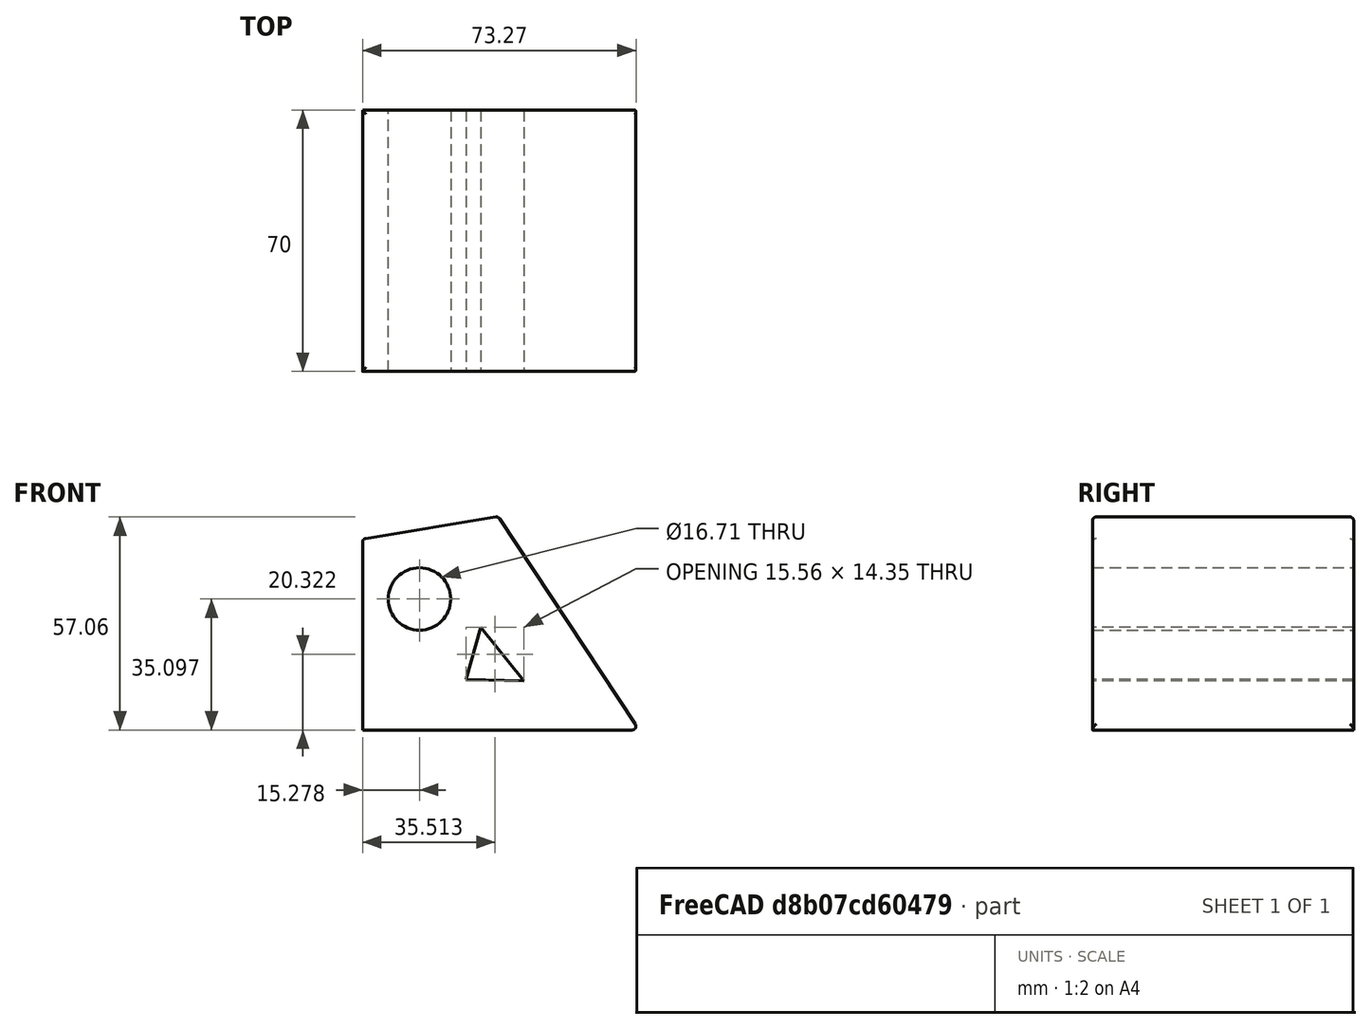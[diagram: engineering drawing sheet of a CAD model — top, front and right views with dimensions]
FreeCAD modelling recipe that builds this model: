
FCSTD DOCUMENT  (FreeCAD 0.19R24366 (Git))
Label: test
License: All rights reserved
LicenseURL: http://en.wikipedia.org/wiki/All_rights_reserved
objects: Sketcher::SketchObject×1, PartDesign::Pad×1, PartDesign::Fillet×1, PartDesign::Hole×1, PartDesign::Body×1
note: 8 computed .brp shape members not serialized (recipe doc carries the construction recipe); baked Part::Feature solids carry a one-line shape summary decoded from their .brp

FEATURE [Sketcher::SketchObject] Sketch
  FullyConstrained = false
  MapMode = 5
  Placement = pos=(0,0,0) rot=(1,0,0;1.5708rad)
  Support = -> [XZ_Plane]
  sketch-geometry (8):
    g0: LineSegment StartX=-60.6306 StartY=73.8594 StartZ=0 EndX=-60.6306 EndY=22.6881 EndZ=0
    g1: LineSegment StartX=-60.6306 StartY=22.6881 StartZ=0 EndX=13.4961 EndY=22.6881 EndZ=0
    g2: LineSegment StartX=13.4961 StartY=22.6881 StartZ=0 EndX=-24.2846 EndY=79.8374 EndZ=0
    g3: LineSegment StartX=-24.2846 StartY=79.8374 StartZ=0 EndX=-60.6306 EndY=73.8594 EndZ=0
    g4: Circle CenterX=-45.3524 CenterY=57.7869 CenterZ=0 NormalX=0 NormalY=0 NormalZ=1 AngleXU=0 Radius=8.35448
    g5: LineSegment StartX=-28.9518 StartY=50.1895 StartZ=0 EndX=-32.8966 EndY=36.1638 EndZ=0
    g6: LineSegment StartX=-17.3368 StartY=35.8351 StartZ=0 EndX=-32.8966 EndY=36.1638 EndZ=0
    g7: LineSegment StartX=-17.3368 StartY=35.8351 StartZ=0 EndX=-28.9518 EndY=50.1895 EndZ=0
  constraints (9):
    c: Vertical(g0)
    c: Coincident(g1,g0)
    c: Horizontal(g1)
    c: Coincident(g2,g1)
    c: Coincident(g3,g2)
    c: Coincident(g3,g0)
    c: Coincident(g6,g5)
    c: Coincident(g7,g6)
    c: Coincident(g7,g5)
FEATURE [PartDesign::Pad] Pad
  Direction = (1,1,1)
  Length = 70
  Length2 = 100
  Placement = pos=(0,0,0) rot=(1,0,0;1.5708rad)
  Profile = -> Sketch
  Type = 0
FEATURE [PartDesign::Fillet] Fillet
  Base = -> Pad [Face3,Face4]
  BaseFeature = -> Pad
  Placement = pos=(0,0,0) rot=(1,0,0;1.5708rad)
  Radius = 1
  SupportTransform = false
FEATURE [PartDesign::Hole] Hole
  BaseFeature = -> Fillet
  Depth = 25
  DepthType = 0
  Diameter = 2.3
  DrillForDepth = false
  DrillPoint = 1
  DrillPointAngle = 118
  HoleCutCountersinkAngle = 90
  HoleCutCustomValues = false
  HoleCutDepth = 0
  HoleCutDiameter = 6.1
  HoleCutType = 0
  ModelActualThread = false
  Placement = pos=(0,0,0) rot=(1,0,0;1.5708rad)
  Profile = -> Fillet [Face1]
  Tapered = false
  TaperedAngle = 90
  ThreadAngle = 0
  ThreadClass = 0
  ThreadCutOffInner = 0
  ThreadCutOffOuter = 0
  ThreadDirection = 0
  ThreadFit = 0
  ThreadPitch = 0
  ThreadSize = 0
  ThreadType = 3
  Threaded = false
FEATURE [PartDesign::Body] Body
  Group = -> [Sketch,Pad,Fillet,Hole]
  Origin = -> Origin
  Tip = -> Hole
